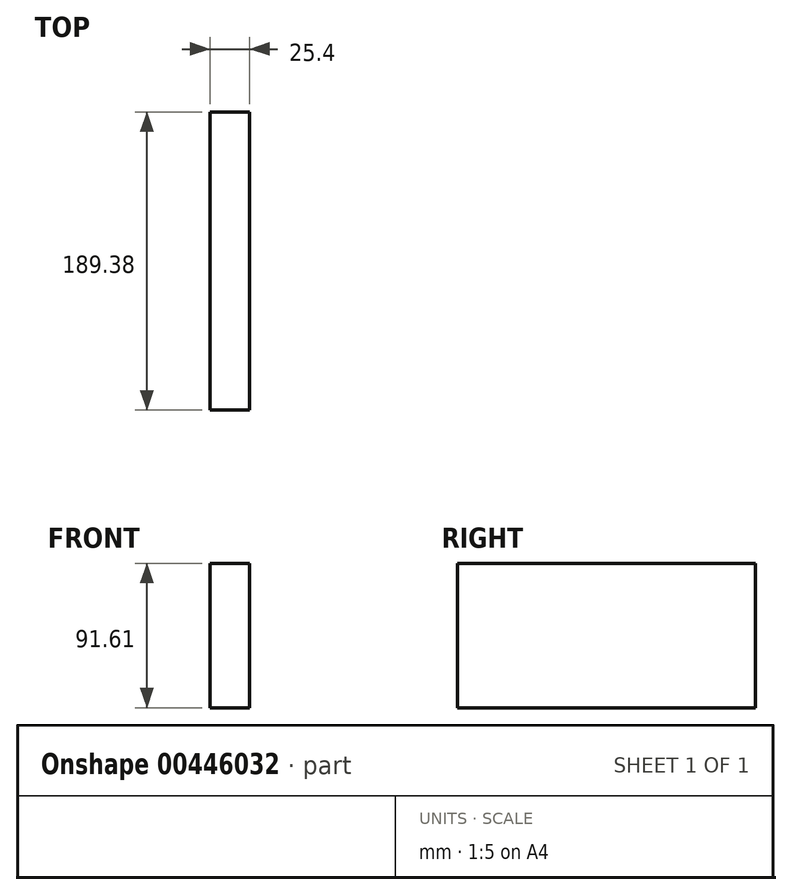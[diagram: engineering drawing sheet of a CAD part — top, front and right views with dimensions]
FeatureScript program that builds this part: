
annotation { "Feature Type Name" : "Feature", "Feature Type Description" : "" }
export const myFeature = defineFeature(function(context is Context, id is Id, definition is map)
    precondition{}
    {
        {
            var Q0;
            Q0=qCreatedBy(makeId("Right.planeOp"),FACE);
            var sketch = newSketch(context, id + "F0", { "sketchPlane" : qUnion([Q0])});
            skLineSegment(sketch, "E0.bottom", {"start": v(-84.53, 174.5) * mm, "end": v(17.1, 174.5) * mm});
            skLineSegment(sketch, "E0.top", {"start": v(-84.53, -123.63) * mm, "end": v(17.1, -123.63) * mm});
            skLineSegment(sketch, "E0.left", {"start": v(-84.53, 174.5) * mm, "end": v(-84.53, -123.63) * mm});
            skLineSegment(sketch, "E0.right", {"start": v(17.1, 174.5) * mm, "end": v(17.1, -123.63) * mm});
            skPoint(sketch, "E0.middle", {"position": v(-33.72, 25.43) * mm});
            skLineSegment(sketch, "E1.bottom", {"start": v(0, 25.43) * mm, "end": v(-83.11, 25.43) * mm});
            skLineSegment(sketch, "E1.top", {"start": v(0, -0.56) * mm, "end": v(-83.11, -0.56) * mm});
            skLineSegment(sketch, "E1.left", {"start": v(0, 25.43) * mm, "end": v(0, -0.56) * mm});
            skLineSegment(sketch, "E1.right", {"start": v(-83.11, 25.43) * mm, "end": v(-83.11, -0.56) * mm});
            skPoint(sketch, "E1.middle", {"position": v(-41.56, 12.43) * mm});
            skPoint(sketch, "E1.cornerSnap0", {"position": v(17.1, 25.43) * mm});
            skLineSegment(sketch, "E2.bottom", {"start": v(262.35, 105.86) * mm, "end": v(72.97, 105.86) * mm});
            skLineSegment(sketch, "E2.top", {"start": v(262.35, 197.47) * mm, "end": v(72.97, 197.47) * mm});
            skLineSegment(sketch, "E2.left", {"start": v(262.35, 105.86) * mm, "end": v(262.35, 197.47) * mm});
            skLineSegment(sketch, "E2.right", {"start": v(72.97, 105.86) * mm, "end": v(72.97, 197.47) * mm});
            skPoint(sketch, "E2.middle", {"position": v(167.66, 151.66) * mm});
            skLineSegment(sketch, "E3.bottom", {"start": v(-170.85, 105.86) * mm, "end": v(-59.45, 105.86) * mm});
            skLineSegment(sketch, "E3.top", {"start": v(-170.85, -136.87) * mm, "end": v(-59.45, -136.87) * mm});
            skLineSegment(sketch, "E3.left", {"start": v(-170.85, 105.86) * mm, "end": v(-170.85, -136.87) * mm});
            skLineSegment(sketch, "E3.right", {"start": v(-59.45, 105.86) * mm, "end": v(-59.45, -136.87) * mm});
            skPoint(sketch, "E3.middle", {"position": v(-115.15, -15.5) * mm});
            skSolve(sketch);
        }
        {
            var Q0;
            Q0=makeQuery(id+"F0.imprint","IMPRINT",FACE,{"disambiguationData":[TD([[makeQuery(id+"F0.imprint","IMPRINT",EDGE,{"derivedFrom":sQuery(id+"F0.wireOp",EDGE,"E2.bottom")}),-1.0]])]});
            extrude(context, id + "F1", {"entities" : qUnion([Q0]), "depth" : 25.4 * mm});
        }
    });
